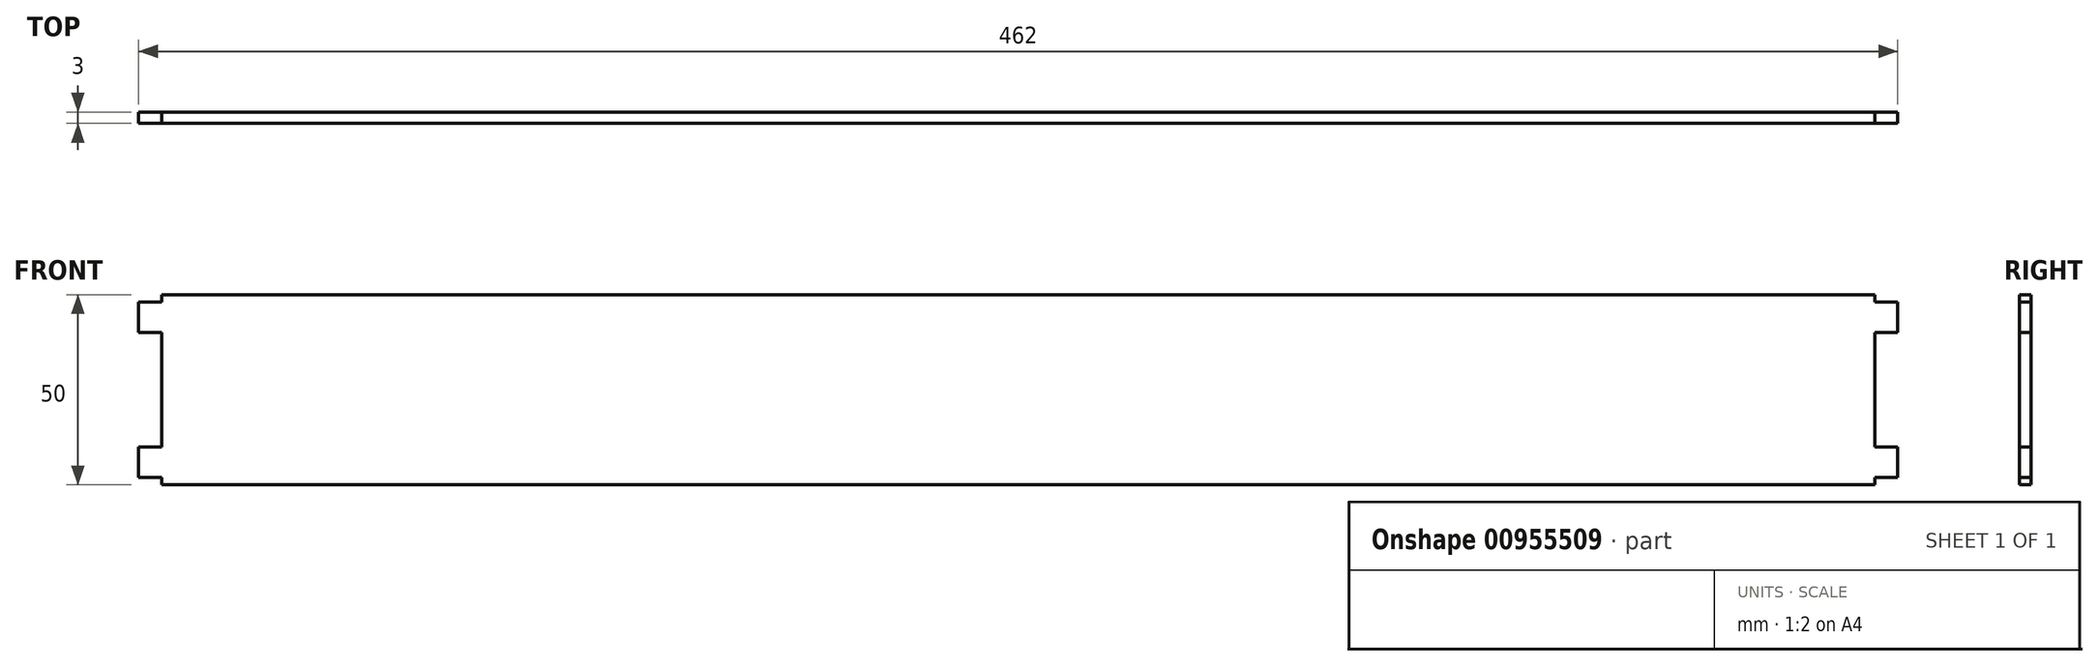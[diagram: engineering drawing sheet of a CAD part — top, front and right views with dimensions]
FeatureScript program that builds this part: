
annotation { "Feature Type Name" : "Feature", "Feature Type Description" : "" }
export const myFeature = defineFeature(function(context is Context, id is Id, definition is map)
    precondition{}
    {
        {
            var Q0;
            Q0=qCreatedBy(makeId("Front.planeOp"),FACE);
            var sketch = newSketch(context, id + "F0", { "sketchPlane" : qUnion([Q0])});
            skLineSegment(sketch, "E0.bottom", {"start": v(-59.97, 1.46) * mm, "end": v(390.03, 1.46) * mm});
            skLineSegment(sketch, "E0.top", {"start": v(-59.97, 51.46) * mm, "end": v(390.03, 51.46) * mm});
            skLineSegment(sketch, "E0.left", {"start": v(-59.97, 1.46) * mm, "end": v(-59.97, 3.46) * mm});
            skLineSegment(sketch, "E0.right", {"start": v(390.03, 1.46) * mm, "end": v(390.03, 3.46) * mm});
            skLineSegment(sketch, "E1.bottom", {"start": v(-59.97, 49.46) * mm, "end": v(-65.97, 49.46) * mm});
            skLineSegment(sketch, "E1.top", {"start": v(-59.97, 41.46) * mm, "end": v(-65.97, 41.46) * mm});
            skLineSegment(sketch, "E1.right", {"start": v(-65.97, 49.46) * mm, "end": v(-65.97, 41.46) * mm});
            skLineSegment(sketch, "E2.0.1.0", {"start": v(-59.97, 11.46) * mm, "end": v(-65.97, 11.46) * mm});
            skLineSegment(sketch, "E2.0.1.1", {"start": v(-65.97, 11.46) * mm, "end": v(-65.97, 3.46) * mm});
            skLineSegment(sketch, "E2.0.1.2", {"start": v(-59.97, 3.46) * mm, "end": v(-65.97, 3.46) * mm});
            skLineSegment(sketch, "E2.1.0.0", {"start": v(396.03, 49.46) * mm, "end": v(390.03, 49.46) * mm});
            skLineSegment(sketch, "E2.1.0.2", {"start": v(396.03, 41.46) * mm, "end": v(390.03, 41.46) * mm});
            skLineSegment(sketch, "E2.1.0.3", {"start": v(396.03, 49.46) * mm, "end": v(396.03, 41.46) * mm});
            skLineSegment(sketch, "E2.1.1.0", {"start": v(396.03, 11.46) * mm, "end": v(390.03, 11.46) * mm});
            skLineSegment(sketch, "E2.1.1.2", {"start": v(396.03, 3.46) * mm, "end": v(390.03, 3.46) * mm});
            skLineSegment(sketch, "E2.1.1.3", {"start": v(396.03, 11.46) * mm, "end": v(396.03, 3.46) * mm});
            skLineSegment(sketch, "E2.direction1", {"start": v(-65.97, 49.46) * mm, "end": v(390.03, 49.46) * mm, "construction": true});
            skLineSegment(sketch, "E2.direction2", {"start": v(-65.97, 49.46) * mm, "end": v(-65.97, 11.46) * mm, "construction": true});
            skLineSegment(sketch, "E3.trimOffspring", {"start": v(-59.97, 49.46) * mm, "end": v(-59.97, 51.46) * mm});
            skLineSegment(sketch, "E4.trimOffspring", {"start": v(-59.97, 11.46) * mm, "end": v(-59.97, 41.46) * mm});
            skLineSegment(sketch, "E5.trimOffspring", {"start": v(390.03, 49.46) * mm, "end": v(390.03, 51.46) * mm});
            skLineSegment(sketch, "E6.trimOffspring", {"start": v(390.03, 11.46) * mm, "end": v(390.03, 41.46) * mm});
            skSolve(sketch);
        }
        {
            var Q0;
            Q0 = qSketchRegion(id + "F0", true);
            extrude(context, id + "F1", {"entities" : qUnion([Q0]), "depth" : 3 * mm, "offsetDistance" : 25 * mm});
        }
    });
